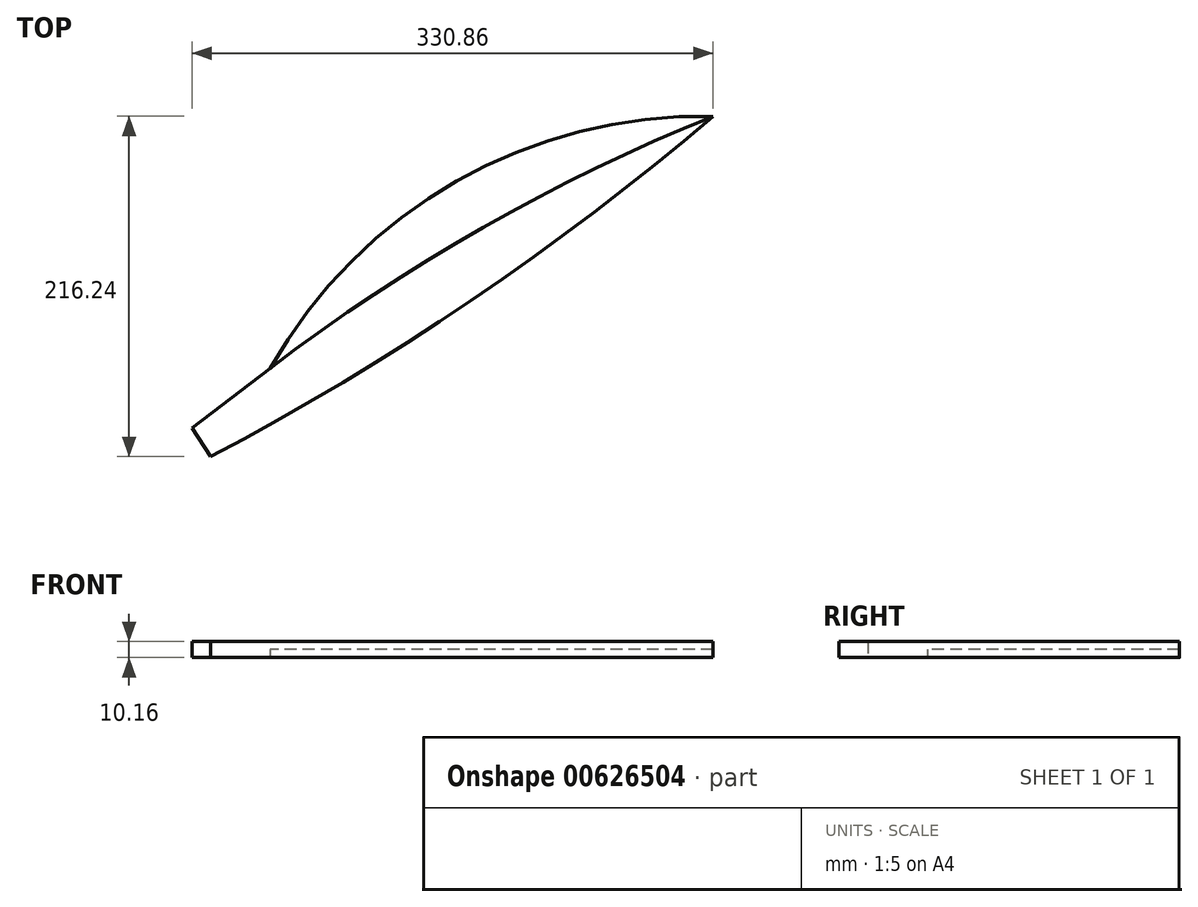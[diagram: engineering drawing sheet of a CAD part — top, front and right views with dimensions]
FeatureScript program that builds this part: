
annotation { "Feature Type Name" : "Feature", "Feature Type Description" : "" }
export const myFeature = defineFeature(function(context is Context, id is Id, definition is map)
    precondition{}
    {
        {
            var Q0;
            Q0=qCreatedBy(makeId("Top.planeOp"),FACE);
            var sketch = newSketch(context, id + "F0", { "sketchPlane" : qUnion([Q0])});
            skPoint(sketch, "E0.middle", {"position": v(0, 0) * mm});
            skPoint(sketch, "E0.top.end.orphan", {"position": v(-162.52, 103.5) * mm});
            skPoint(sketch, "E0.left.start.orphan", {"position": v(162.52, -103.5) * mm});
            skLineSegment(sketch, "E1", {"start": v(-162.52, -103.5) * mm, "end": v(-156.7, -112.66) * mm});
            skLineSegment(sketch, "E2.MirrorCS", {"start": v(-162.52, -103.5) * mm, "end": v(-168.34, -94.36) * mm});
            skLineSegment(sketch, "E3.MirrorCS", {"start": v(-168.34, -94.36) * mm, "end": v(-118.8, -56.58) * mm});
            skArc(sketch, "E4", {"start": v(162.52, 103.5) * mm, "mid": v(-0.26, 62.33) * mm, "end": v(-118.8, -56.58) * mm});
            skArc(sketch, "E5", {"start": v(-156.7, -112.66) * mm, "mid": v(9, -13.55) * mm, "end": v(162.52, 103.5) * mm});
            skSolve(sketch);
        }
        {
            var Q0;
            Q0 = qSketchRegion(id + "F0", true);
            extrude(context, id + "F1", {"entities" : qUnion([Q0]), "depth" : 10.16 * mm, "offsetDistance" : 25.4 * mm});
        }
        {
            var Q0;
            Q0=makeQuery(id+"F1.opExtrude","CAP_FACE",FACE,{"disambiguationData":[OSD([sQuery(id+"F0.wireOp",EDGE,"E1"),sQuery(id+"F0.wireOp",EDGE,"E2.MirrorCS"),sQuery(id+"F0.wireOp",EDGE,"E3.MirrorCS"),sQuery(id+"F0.wireOp",EDGE,"E4"),sQuery(id+"F0.wireOp",EDGE,"E5")])],"isStart":false});
            var sketch = newSketch(context, id + "F2", { "sketchPlane" : qUnion([Q0])});
            skArc(sketch, "E6", {"start": v(162.52, 103.5) * mm, "mid": v(-0.3, 62.39) * mm, "end": v(-118.8, -56.58) * mm});
            skArc(sketch, "E7", {"start": v(162.52, 103.5) * mm, "mid": v(16.5, 32.9) * mm, "end": v(-118.8, -56.58) * mm});
            skSolve(sketch);
        }
        {
            var Q0;
            Q0 = qSketchRegion(id + "F2", true);
            extrude(context, id + "F3", {"entities" : qUnion([Q0]), "operationType" : NewBodyOperationType.REMOVE, "oppositeDirection" : true, "depth" : 5.08 * mm, "offsetDistance" : 25.4 * mm});
        }
    });
